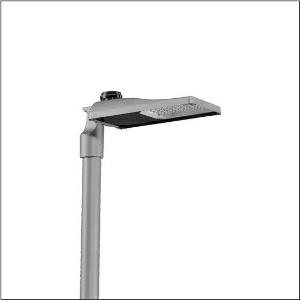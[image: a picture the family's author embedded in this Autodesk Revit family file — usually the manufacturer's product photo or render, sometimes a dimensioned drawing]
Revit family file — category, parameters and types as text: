
# Revit family: streetlight_sl_31_mini___st1_0a_5xh6d35n08ja_1cc2
name_source: partatom
category: Lighting Fixtures
units: mm (PartAtom-declared; Revit-internal decimal feet)

## family parameters
Cut with Voids When Loaded = No
Host = Face
Light Source = No
Part Type = Normal
Room Calculation Point = No
Round Connector Dimension = Use Diameter
Shared = No

## types (1)
- --- (1 x LED, 12140 lm, 81.1 W, 3000K)
    Apparent Load = 81 VA
    CIE Flux Codes = 40 73 97 100 100
    Color Rendering = 70
    Color Temperature = 3000K
    Default Elevation = 1800 mm
    Description = Streetlight SL 31 mini NEMA (7pin), Desk-Remote mast luminaire for post-top, side-entry; light control with lens of PMMA; light distribution: ST1.0a, direct asymmetric distribution, for standard-compliant lighting for roads and squares; LED: luminous flux: 12.140lm, light colour: 730, colour temperature: 3000K; luminous efficacy: 149,7lm/W; control: pre-setting: linear dimming characteristic, flexible luminous flux parameterisation, time-dependent luminous flux control, constant luminous flux control, intelligent temperature release in ECG and LED module, overheat protection; luminaire housing, of diecast aluminium, SITECO metallic grey (DB 702S), corrosivity category C5 high according to DIN EN ISO 12944; cover of toughened safety glass, transparent, opened without tools; mast flange of diecast aluminium, SITECO metallic grey (DB 702S), spigot size: 76/60mm, mast flange included unmounted; cable length: 10,5m, connection cable pre-assembled; mains connection: 220..240V, AC, 50/60Hz; power consumption (at start of service life): 81,1W / (at end of service life): 88,3W / (with reduced operation 50%): 36,4W; protection rating (complete): IP66; insulation class (complete): insulation class I (protective earthing); impact resistance: IK10; certification: CE, ENEC, ENEC+, VDE, UKCA; permissible operating ambient temperature for outdoor applications: -40..+50°C; packaging unit: 1 piece

Light Distribution: ST1.0a
    Height = 76 mm
    Lamp = 1 x LED
    Lamp Light Flux = 12140 lm
    Lamp Power = 81.1 W
    Lamp count = 1
    Length = 547 mm
    Luminous efficacy = 150 lm/W
    Manufacturer = Siteco
    ModVariant = No
    Model = 5XH6D35N08JA
    Number of Poles = 1
    OnlyDefault = Yes
    Power Factor = 1
    Product Name = Streetlight SL 31 mini | ST1.0a
    Product group = mast luminaire | pylon top
    ProductGroupID = 6100
    Protection Class = Protection class I
    Protection Degree = IP 66
    RLX_Detail_Level = 1
    RLX_Emergency_Light_Flux = 0 lm
    RLX_Emergency_Type = 0
    RLX_Emergency_Type_DB = No
    RlxData = <blob elided: 40297 chars, md5=b7c7736d>
    Socket = socket
    Standby Power = 0 W
    System Light Flux = 12140 lm
    System Power = 81 W
    Type Comments = factory setting: luminous flux: 100 % | dim-lin: 254 | 860 mA
    Type Image = l_1300322.jpg
    URL = http://relux.com
    VarID = @adj_056995
    Voltage = 0 V
    Weight = 0.00 kg
    Width = 265 mm

## geometry (parser evidence)
native form markers: Blend x4, Sweep x10
no freeform markers — native parametric forms only
